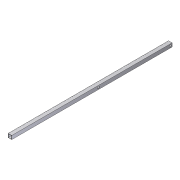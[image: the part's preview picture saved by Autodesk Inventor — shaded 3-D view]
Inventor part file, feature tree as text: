
AUTODESK INVENTOR PART (.ipt)
format: ipt  version: 2012 (Build 160160000, 160)  size: 92,160 bytes
history: native  units: in
note: dims shown in document units (in); Inventor stores cm internally (conversion verified against a paired STEP export)
features: extrude x3, sketch x3, shell x1
ambient origin geometry x8: Origin, YZ Plane, XZ Plane, XY Plane, X Axis, Y Axis, Z Axis, Center Point
bodies: Solid1 (feature_tree)
feature tree (7):
  extrude  "Extrusion1"  Depth=1.75in
  shell  "Shell1"  Thickness=78.0in
  extrude  "Extrusion2"  Depth=1.4375in
  extrude  "Extrusion4"  Depth=0.875in
  sketch  "Sketch1"  dims[d0=1.75in d1=1.75in d2=78.0in d3=0.0in]
  sketch  "Sketch2"  dims[d4=0.125in d5=1.4375in]
  sketch  "Sketch4"  dims[d6=1.75in d7=0.875in d9=78.0in d10=0.0in d16=1.4375in d17=0.875in d18=35.0in d20=1.0in d21=0.125in d22=0.0in d23=1.0in]
